# Revit family: CFAB - Ceiling and Wall Panels
name_source: partatom
category: Generic Models
revit_build: Autodesk Revit 2016 (Build: 20150220_1215(x64)
units: mm (PartAtom-declared; Revit-internal decimal feet)

## family parameters
Always vertical = No
Can host rebar = No
Cut with Voids When Loaded = No
Part Type = Normal
Room Calculation Point = No
Round Connector Dimension = Use Diameter
Shared = No
Work Plane-Based = Yes

## types (15) — shared parameters
A = 0' - 0"
Default Elevation = 4' - 0"
Finish = CFAB
Manufacturer = Acoustical Surfaces, Inc.
Material = CFAB - Cellulose Absorptive Acoustical Panels
URL = https://www.acousticalsurfaces.com

## per-type parameters (varying)
| type | Length | T | Thickness Options | Width | ‍      0. Thickness 1" | ‍      1. Thickness 1 1/2" | ‍      2. Thickness 2" |
| 2 INCH - 48X96 | 4' - 0" | 0' - 2" | 2 | 8' - 0" | No | No | Yes |
| 1.5 INCH - 48X96 | 4' - 0" | 0' - 1 1/2" | 1 | 8' - 0" | No | Yes | No |
| 1 INCH - 48X96 | 4' - 0" | 0' - 1" | 0 | 8' - 0" | Yes | No | No |
| 2 INCH - 48X48 | 4' - 0" | 0' - 2" | 2 | 4' - 0" | No | No | Yes |
| 1.5 INCH - 48X48 | 4' - 0" | 0' - 1 1/2" | 1 | 4' - 0" | No | Yes | No |
| 1 INCH - 48X48 | 4' - 0" | 0' - 1" | 0 | 4' - 0" | Yes | No | No |
| 2 INCH - 24X24 | 2' - 0" | 0' - 2" | 2 | 2' - 0" | No | No | Yes |
| 1.5 INCH - 24X24 | 2' - 0" | 0' - 1 1/2" | 1 | 2' - 0" | No | Yes | No |
| 1 INCH - 24X24 | 2' - 0" | 0' - 1" | 0 | 2' - 0" | Yes | No | No |
| 2 INCH - 12X12 | 1' - 0" | 0' - 2" | 2 | 1' - 0" | No | No | Yes |
| 1.5 INCH - 12X12 | 1' - 0" | 0' - 1 1/2" | 1 | 1' - 0" | No | Yes | No |
| 1 INCH - 12X12 | 1' - 0" | 0' - 1" | 0 | 1' - 0" | Yes | No | No |
| 2 INCH - 24x48 | 4' - 0" | 0' - 2" | 2 | 2' - 0" | No | No | Yes |
| 1.5 INCH - 24x48 | 4' - 0" | 0' - 1 1/2" | 1 | 2' - 0" | No | Yes | No |
| 1 INCH - 24x48 | 4' - 0" | 0' - 1" | 0 | 2' - 0" | Yes | No | No |

## geometry (parser evidence)
native form markers: Sweep x8
no freeform markers — native parametric forms only
